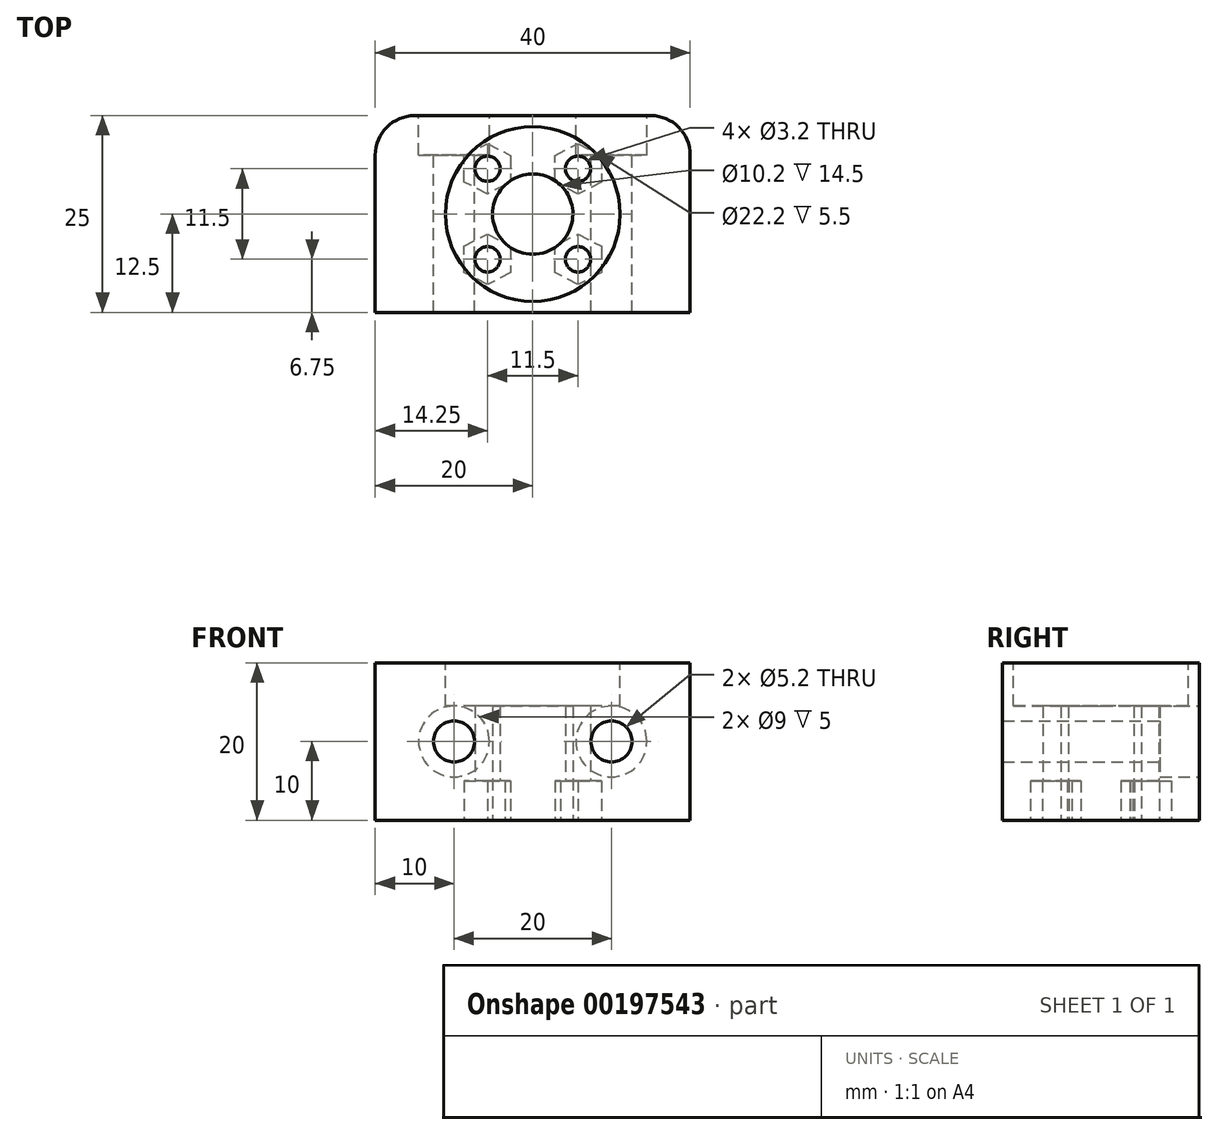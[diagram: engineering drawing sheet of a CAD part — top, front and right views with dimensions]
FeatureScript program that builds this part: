
annotation { "Feature Type Name" : "Feature", "Feature Type Description" : "" }
export const myFeature = defineFeature(function(context is Context, id is Id, definition is map)
    precondition{}
    {
        {
            var Q0;
            Q0=qCreatedBy(makeId("Top.planeOp"),FACE);
            var sketch = newSketch(context, id + "F0", { "sketchPlane" : qUnion([Q0])});
            skCircle(sketch, "E0", {"center": v(0, 0) * mm, "radius": 11 * mm, "construction": true});
            skCircle(sketch, "E1", {"center": v(0, 0) * mm, "radius": 5.1 * mm});
            skLineSegment(sketch, "E2.bottom", {"start": v(-5.75, 5.75) * mm, "end": v(5.75, 5.75) * mm, "construction": true});
            skLineSegment(sketch, "E2.top", {"start": v(-5.75, -5.75) * mm, "end": v(5.75, -5.75) * mm, "construction": true});
            skLineSegment(sketch, "E2.left", {"start": v(-5.75, 5.75) * mm, "end": v(-5.75, -5.75) * mm, "construction": true});
            skLineSegment(sketch, "E2.right", {"start": v(5.75, 5.75) * mm, "end": v(5.75, -5.75) * mm, "construction": true});
            skCircle(sketch, "E3", {"center": v(5.75, 5.75) * mm, "radius": 1.6 * mm});
            skCircle(sketch, "E4", {"center": v(-5.75, 5.75) * mm, "radius": 1.6 * mm});
            skCircle(sketch, "E5", {"center": v(5.75, -5.75) * mm, "radius": 1.6 * mm});
            skCircle(sketch, "E6", {"center": v(-5.75, -5.75) * mm, "radius": 1.6 * mm});
            skLineSegment(sketch, "E7.bottom", {"start": v(-20, 12.5) * mm, "end": v(20, 12.5) * mm});
            skLineSegment(sketch, "E7.top", {"start": v(-20, -12.5) * mm, "end": v(20, -12.5) * mm});
            skLineSegment(sketch, "E7.left", {"start": v(-20, 12.5) * mm, "end": v(-20, -12.5) * mm});
            skLineSegment(sketch, "E7.right", {"start": v(20, 12.5) * mm, "end": v(20, -12.5) * mm});
            skSolve(sketch);
        }
        {
            var Q0;
            Q0=qSketchRegion(id+"F0",true);
            extrude(context, id + "F1", {"entities" : qUnion([Q0]), "depth" : 20 * mm});
        }
        {
            var Q0;
            Q0=makeQuery(id+"F1.opExtrude","SWEPT_EDGE",EDGE,{"disambiguationData":[OSD([sQuery(id+"F0.wireOp",EDGE,"E7.bottom"),sQuery(id+"F0.wireOp",EDGE,"E7.right")])]});
            var Q1;
            Q1=makeQuery(id+"F1.opExtrude","SWEPT_EDGE",EDGE,{"disambiguationData":[OSD([sQuery(id+"F0.wireOp",EDGE,"E7.bottom"),sQuery(id+"F0.wireOp",EDGE,"E7.left")])]});
            fillet(context, id + "F2", {"entities" : qUnion([Q0, Q1]), "radius" : 5 * mm, "tangentPropagation" : true, "allowEdgeOverflow" : false});
        }
        {
            var Q0;
            Q0=makeQuery(id+"F1.opExtrude","CAP_FACE",FACE,{"disambiguationData":[OSD([sQuery(id+"F0.wireOp",EDGE,"E1"),sQuery(id+"F0.wireOp",EDGE,"E3"),sQuery(id+"F0.wireOp",EDGE,"E4"),sQuery(id+"F0.wireOp",EDGE,"E5"),sQuery(id+"F0.wireOp",EDGE,"E6"),sQuery(id+"F0.wireOp",EDGE,"E7.bottom"),sQuery(id+"F0.wireOp",EDGE,"E7.top"),sQuery(id+"F0.wireOp",EDGE,"E7.left"),sQuery(id+"F0.wireOp",EDGE,"E7.right")])],"isStart":false});
            var sketch = newSketch(context, id + "F3", { "sketchPlane" : qUnion([Q0])});
            skCircle(sketch, "E8", {"center": v(0, 0) * mm, "radius": 11.1 * mm});
            skSolve(sketch);
        }
        {
            var Q0;
            Q0=qSketchRegion(id+"F3",true);
            extrude(context, id + "F4", {"entities" : qUnion([Q0]), "operationType" : NewBodyOperationType.REMOVE, "oppositeDirection" : true, "depth" : 5.5 * mm});
        }
        {
            var Q0;
            Q0=makeQuery(id+"F1.opExtrude","CAP_FACE",FACE,{"disambiguationData":[OSD([sQuery(id+"F0.wireOp",EDGE,"E1"),sQuery(id+"F0.wireOp",EDGE,"E3"),sQuery(id+"F0.wireOp",EDGE,"E4"),sQuery(id+"F0.wireOp",EDGE,"E5"),sQuery(id+"F0.wireOp",EDGE,"E6"),sQuery(id+"F0.wireOp",EDGE,"E7.bottom"),sQuery(id+"F0.wireOp",EDGE,"E7.top"),sQuery(id+"F0.wireOp",EDGE,"E7.left"),sQuery(id+"F0.wireOp",EDGE,"E7.right")])],"isStart":true});
            var sketch = newSketch(context, id + "F5", { "sketchPlane" : qUnion([Q0])});
            skCircle(sketch, "E9", {"center": v(5.75, 5.75) * mm, "radius": 2.75 * mm, "construction": true});
            skLineSegment(sketch, "E10", {"start": v(5.75, 11.03) * mm, "end": v(5.75, 0.94) * mm, "construction": true});
            skLineSegment(sketch, "E11", {"start": v(5.75, 5.75) * mm, "end": v(1.68, 5.75) * mm, "construction": true});
            skLineSegment(sketch, "E12", {"start": v(5.75, 5.75) * mm, "end": v(10.33, 5.75) * mm, "construction": true});
            skLineSegment(sketch, "E13", {"start": v(8.5, 7.3) * mm, "end": v(8.5, 4.2) * mm, "construction": true});
            skLineSegment(sketch, "E14", {"start": v(8.5, 4.2) * mm, "end": v(5.75, 2.76) * mm, "construction": true});
            skLineSegment(sketch, "E15", {"start": v(5.75, 2.76) * mm, "end": v(3, 4.2) * mm, "construction": true});
            skLineSegment(sketch, "E16", {"start": v(3, 4.2) * mm, "end": v(3, 7.3) * mm, "construction": true});
            skLineSegment(sketch, "E17", {"start": v(3, 7.3) * mm, "end": v(5.75, 8.74) * mm, "construction": true});
            skLineSegment(sketch, "E18", {"start": v(5.75, 8.74) * mm, "end": v(8.5, 7.3) * mm, "construction": true});
            skLineSegment(sketch, "E19", {"start": v(5.74, 8.98) * mm, "end": v(2.8, 7.44) * mm});
            skLineSegment(sketch, "E20", {"start": v(2.8, 7.44) * mm, "end": v(2.8, 4.08) * mm});
            skLineSegment(sketch, "E21", {"start": v(2.8, 4.08) * mm, "end": v(5.75, 2.53) * mm});
            skLineSegment(sketch, "E22", {"start": v(5.75, 2.53) * mm, "end": v(8.7, 4.08) * mm});
            skLineSegment(sketch, "E23", {"start": v(8.7, 4.08) * mm, "end": v(8.7, 7.42) * mm});
            skLineSegment(sketch, "E24", {"start": v(8.7, 7.42) * mm, "end": v(5.74, 8.98) * mm});
            skCircle(sketch, "E25.0", {"center": v(5.75, 5.75) * mm, "radius": 1.6 * mm, "construction": true});
            skCircle(sketch, "E26", {"center": v(5.75, -5.75) * mm, "radius": 2.75 * mm, "construction": true});
            skLineSegment(sketch, "E27", {"start": v(5.75, -0.47) * mm, "end": v(5.75, -10.56) * mm, "construction": true});
            skLineSegment(sketch, "E28", {"start": v(5.75, -5.75) * mm, "end": v(1.68, -5.75) * mm, "construction": true});
            skLineSegment(sketch, "E29", {"start": v(5.75, -5.75) * mm, "end": v(10.33, -5.75) * mm, "construction": true});
            skLineSegment(sketch, "E30", {"start": v(8.5, -4.2) * mm, "end": v(8.5, -7.3) * mm, "construction": true});
            skLineSegment(sketch, "E31", {"start": v(8.5, -7.3) * mm, "end": v(5.75, -8.74) * mm, "construction": true});
            skLineSegment(sketch, "E32", {"start": v(5.75, -8.74) * mm, "end": v(3, -7.3) * mm, "construction": true});
            skLineSegment(sketch, "E33", {"start": v(3, -7.3) * mm, "end": v(3, -4.2) * mm, "construction": true});
            skLineSegment(sketch, "E34", {"start": v(3, -4.2) * mm, "end": v(5.75, -2.76) * mm, "construction": true});
            skLineSegment(sketch, "E35", {"start": v(5.75, -2.76) * mm, "end": v(8.5, -4.2) * mm, "construction": true});
            skLineSegment(sketch, "E36", {"start": v(5.74, -2.52) * mm, "end": v(2.8, -4.06) * mm});
            skLineSegment(sketch, "E37", {"start": v(2.8, -4.06) * mm, "end": v(2.8, -7.42) * mm});
            skLineSegment(sketch, "E38", {"start": v(2.8, -7.42) * mm, "end": v(5.75, -8.97) * mm});
            skLineSegment(sketch, "E39", {"start": v(5.75, -8.97) * mm, "end": v(8.7, -7.42) * mm});
            skLineSegment(sketch, "E40", {"start": v(8.7, -7.42) * mm, "end": v(8.7, -4.08) * mm});
            skLineSegment(sketch, "E41", {"start": v(8.7, -4.08) * mm, "end": v(5.74, -2.52) * mm});
            skCircle(sketch, "E42.0", {"center": v(5.75, -5.75) * mm, "radius": 1.6 * mm});
            skCircle(sketch, "E43.0", {"center": v(-5.75, -5.75) * mm, "radius": 1.6 * mm});
            skCircle(sketch, "E44.0", {"center": v(-5.75, 5.75) * mm, "radius": 1.6 * mm});
            skCircle(sketch, "E45", {"center": v(-5.75, -5.75) * mm, "radius": 2.75 * mm, "construction": true});
            skLineSegment(sketch, "E46", {"start": v(-5.75, -0.47) * mm, "end": v(-5.75, -10.56) * mm, "construction": true});
            skLineSegment(sketch, "E47", {"start": v(-5.75, -5.75) * mm, "end": v(-9.82, -5.75) * mm, "construction": true});
            skLineSegment(sketch, "E48", {"start": v(-5.75, -5.75) * mm, "end": v(-1.17, -5.75) * mm, "construction": true});
            skLineSegment(sketch, "E49", {"start": v(-3, -4.2) * mm, "end": v(-3, -7.3) * mm, "construction": true});
            skLineSegment(sketch, "E50", {"start": v(-3, -7.3) * mm, "end": v(-5.75, -8.74) * mm, "construction": true});
            skLineSegment(sketch, "E51", {"start": v(-5.75, -8.74) * mm, "end": v(-8.5, -7.3) * mm, "construction": true});
            skLineSegment(sketch, "E52", {"start": v(-8.5, -7.3) * mm, "end": v(-8.5, -4.2) * mm, "construction": true});
            skLineSegment(sketch, "E53", {"start": v(-8.5, -4.2) * mm, "end": v(-5.75, -2.76) * mm, "construction": true});
            skLineSegment(sketch, "E54", {"start": v(-5.75, -2.76) * mm, "end": v(-3, -4.2) * mm, "construction": true});
            skLineSegment(sketch, "E55", {"start": v(-5.76, -2.52) * mm, "end": v(-8.7, -4.06) * mm});
            skLineSegment(sketch, "E56", {"start": v(-8.7, -4.06) * mm, "end": v(-8.7, -7.42) * mm});
            skLineSegment(sketch, "E57", {"start": v(-8.7, -7.42) * mm, "end": v(-5.75, -8.97) * mm});
            skLineSegment(sketch, "E58", {"start": v(-5.75, -8.97) * mm, "end": v(-2.8, -7.42) * mm});
            skLineSegment(sketch, "E59", {"start": v(-2.8, -7.42) * mm, "end": v(-2.8, -4.08) * mm});
            skLineSegment(sketch, "E60", {"start": v(-2.8, -4.08) * mm, "end": v(-5.76, -2.52) * mm});
            skCircle(sketch, "E61", {"center": v(-5.75, 5.75) * mm, "radius": 2.75 * mm, "construction": true});
            skLineSegment(sketch, "E62", {"start": v(-5.75, 11.03) * mm, "end": v(-5.75, 0.94) * mm, "construction": true});
            skLineSegment(sketch, "E63", {"start": v(-5.75, 5.75) * mm, "end": v(-9.82, 5.75) * mm, "construction": true});
            skLineSegment(sketch, "E64", {"start": v(-5.75, 5.75) * mm, "end": v(-1.17, 5.75) * mm, "construction": true});
            skLineSegment(sketch, "E65", {"start": v(-3, 7.3) * mm, "end": v(-3, 4.2) * mm, "construction": true});
            skLineSegment(sketch, "E66", {"start": v(-3, 4.2) * mm, "end": v(-5.75, 2.76) * mm, "construction": true});
            skLineSegment(sketch, "E67", {"start": v(-5.75, 2.76) * mm, "end": v(-8.5, 4.2) * mm, "construction": true});
            skLineSegment(sketch, "E68", {"start": v(-8.5, 4.2) * mm, "end": v(-8.5, 7.3) * mm, "construction": true});
            skLineSegment(sketch, "E69", {"start": v(-8.5, 7.3) * mm, "end": v(-5.75, 8.74) * mm, "construction": true});
            skLineSegment(sketch, "E70", {"start": v(-5.75, 8.74) * mm, "end": v(-3, 7.3) * mm, "construction": true});
            skLineSegment(sketch, "E71", {"start": v(-5.76, 8.98) * mm, "end": v(-8.7, 7.44) * mm});
            skLineSegment(sketch, "E72", {"start": v(-8.7, 7.44) * mm, "end": v(-8.7, 4.08) * mm});
            skLineSegment(sketch, "E73", {"start": v(-8.7, 4.08) * mm, "end": v(-5.75, 2.53) * mm});
            skLineSegment(sketch, "E74", {"start": v(-5.75, 2.53) * mm, "end": v(-2.8, 4.08) * mm});
            skLineSegment(sketch, "E75", {"start": v(-2.8, 4.08) * mm, "end": v(-2.8, 7.42) * mm});
            skLineSegment(sketch, "E76", {"start": v(-2.8, 7.42) * mm, "end": v(-5.76, 8.98) * mm});
            skSolve(sketch);
        }
        {
            var Q0;
            Q0=qSketchRegion(id+"F5",true);
            extrude(context, id + "F6", {"entities" : qUnion([Q0]), "operationType" : NewBodyOperationType.REMOVE, "oppositeDirection" : true, "depth" : 5 * mm});
        }
        {
            var Q0;
            Q0=makeQuery(id+"F1.opExtrude","SWEPT_FACE",FACE,{"disambiguationData":[OSD([sQuery(id+"F0.wireOp",EDGE,"E7.bottom")])]});
            var sketch = newSketch(context, id + "F7", { "sketchPlane" : qUnion([Q0])});
            skCircle(sketch, "E77", {"center": v(-10, 10) * mm, "radius": 2.6 * mm});
            skCircle(sketch, "E78", {"center": v(10, 10) * mm, "radius": 2.6 * mm});
            skSolve(sketch);
        }
        {
            var Q0;
            Q0=qSketchRegion(id+"F7",true);
            extrude(context, id + "F8", {"entities" : qUnion([Q0]), "operationType" : NewBodyOperationType.REMOVE, "endBound" : BoundingType.THROUGH_ALL, "oppositeDirection" : true, "depth" : 25 * mm});
        }
        {
            var Q0;
            Q0=makeQuery(id+"F1.opExtrude","SWEPT_FACE",FACE,{"disambiguationData":[OSD([sQuery(id+"F0.wireOp",EDGE,"E7.bottom")])]});
            var sketch = newSketch(context, id + "F9", { "sketchPlane" : qUnion([Q0])});
            skCircle(sketch, "E79.0", {"center": v(-10, 10) * mm, "radius": 2.6 * mm});
            skCircle(sketch, "E80.0", {"center": v(10, 10) * mm, "radius": 2.6 * mm});
            skCircle(sketch, "E81", {"center": v(10, 10) * mm, "radius": 4.5 * mm});
            skCircle(sketch, "E82", {"center": v(-10, 10) * mm, "radius": 4.5 * mm});
            skSolve(sketch);
        }
        {
            var Q0;
            Q0=qSketchRegion(id+"F9",true);
            extrude(context, id + "F10", {"entities" : qUnion([Q0]), "operationType" : NewBodyOperationType.REMOVE, "oppositeDirection" : true, "depth" : 5 * mm});
        }
    });
